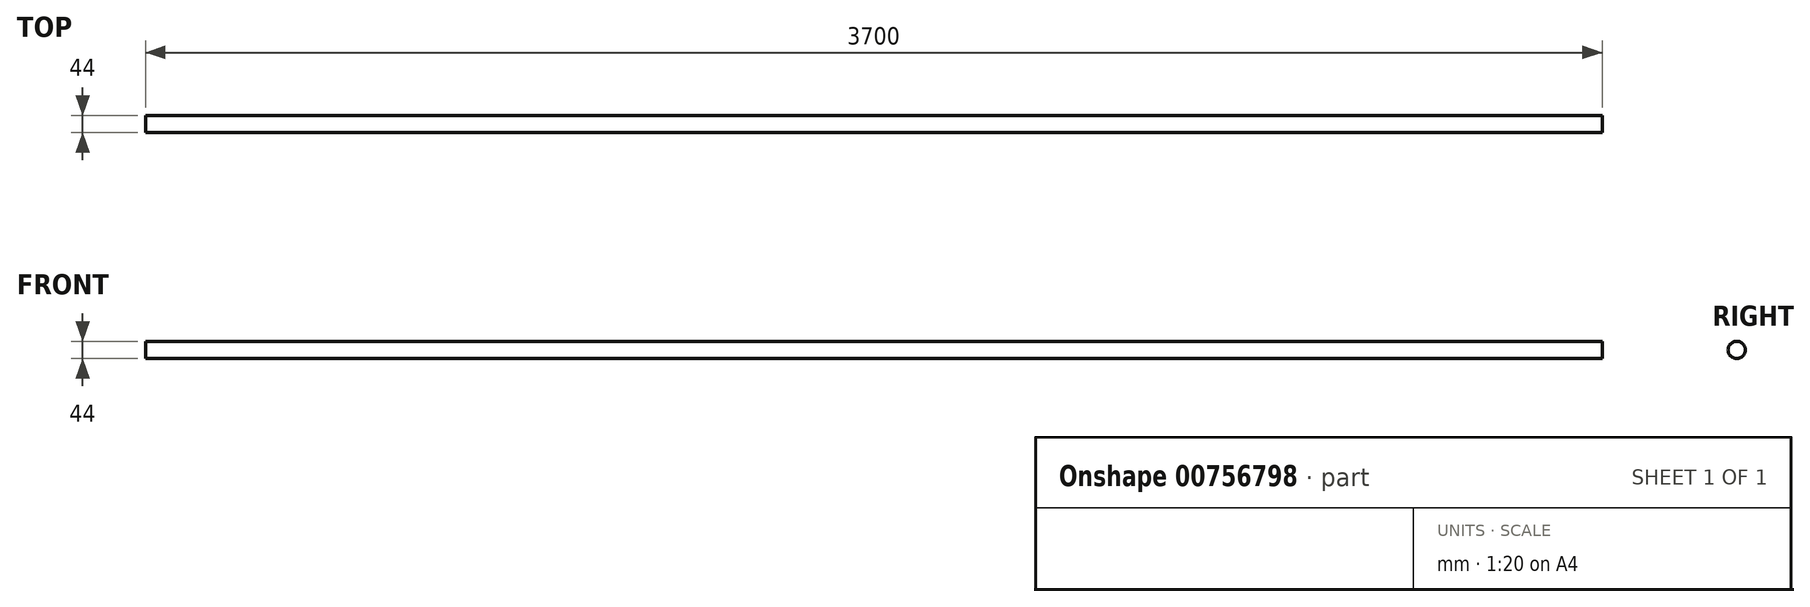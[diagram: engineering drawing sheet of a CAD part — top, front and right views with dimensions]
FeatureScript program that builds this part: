
annotation { "Feature Type Name" : "Feature", "Feature Type Description" : "" }
export const myFeature = defineFeature(function(context is Context, id is Id, definition is map)
    precondition{}
    {
        {
            var Q0;
            Q0=qCreatedBy(makeId("Right.planeOp"),FACE);
            var sketch = newSketch(context, id + "F0", { "sketchPlane" : qUnion([Q0])});
            skCircle(sketch, "E0", {"center": v(-33.57, 30.74) * mm, "radius": 22 * mm});
            skSolve(sketch);
        }
        {
            var Q0;
            Q0 = qSketchRegion(id + "F0", true);
            extrude(context, id + "F1", {"entities" : qUnion([Q0]), "depth" : 3700 * mm, "offsetDistance" : 25 * mm});
        }
    });
